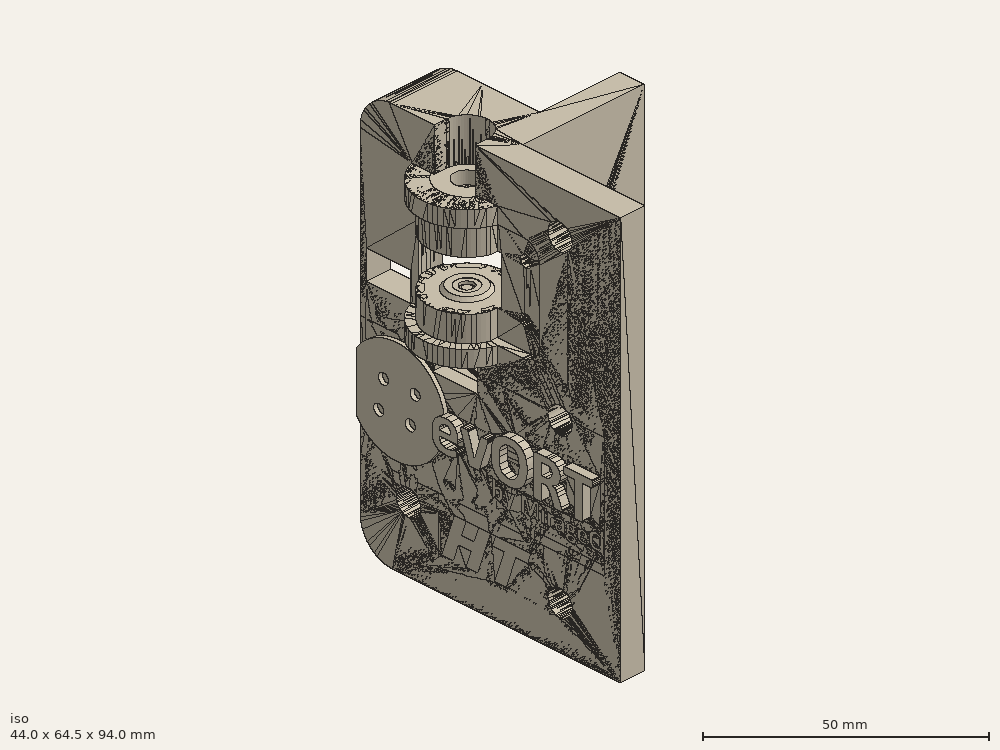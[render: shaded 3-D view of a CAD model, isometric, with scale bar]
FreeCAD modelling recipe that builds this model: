
FCSTD DOCUMENT  (FreeCAD 0.18R16146 (Git))
Label: front-idler-left-2
License: All rights reserved
LicenseURL: http://en.wikipedia.org/wiki/All_rights_reserved
objects: Part::Cylinder×11, Part::Cut×9, Part::Box×8, Part::MultiFuse×8, Part::Chamfer×5, Part::Feature×4
note: 45 computed .brp shape members not serialized (recipe doc carries the construction recipe); baked Part::Feature solids carry a one-line shape summary decoded from their .brp

FEATURE [Part::Feature] Part__Feature  label="PulleyMount_FRONT_LEFT_BodyV1.1"
  Placement = pos=(30,-2.64,-428.83) rot=(1,0,0;1.5708rad)
  shape: bbox 44 x 64.5 x 93.95 mm, 768 faces (baked)
FEATURE [Part::Box] Box  label="Cube"
  AttacherType = Attacher::AttachEngine3D
  Height = 10
  Length = 10
  Placement = pos=(0,7.92,20) rot=(0,0,1;0rad)
  Width = 12
FEATURE [Part::Feature] Part__Feature001  label="PulleyMount_FRONT_LEFT_BodyV1.002"
  shape: bbox 44 x 64.5 x 93.95 mm, 768 faces (baked)
FEATURE [Part::Cut] Cut
  Base = -> Part__Feature001
  Tool = -> Box
FEATURE [Part::Box] Box002  label="Cube002"
  AttacherType = Attacher::AttachEngine3D
  Height = 29
  Length = 3
  Placement = pos=(-1,-8.1,14) rot=(0,0,1;0rad)
  Width = 6.2
FEATURE [Part::Box] Box003  label="Cube003"
  AttacherType = Attacher::AttachEngine3D
  Height = 29
  Length = 3
  Placement = pos=(-1,-8.1,51) rot=(0,0,1;0rad)
  Width = 6.2
FEATURE [Part::Box] Box004  label="Cube004"
  AttacherType = Attacher::AttachEngine3D
  Height = 6.4
  Length = 3
  Placement = pos=(-1,11,12) rot=(0,0,1;0rad)
  Width = 16
FEATURE [Part::Cylinder] Cylinder  label="pos"
  Angle = 360
  AttacherType = Attacher::AttachEngine3D
  Height = 10
  Placement = pos=(-3,20.86,51.94) rot=(0,0,1;0rad)
  Radius = 1
FEATURE [Part::Cylinder] Cylinder001  label="pos001"
  Angle = 360
  AttacherType = Attacher::AttachEngine3D
  Height = 9.75
  Placement = pos=(-3,20.86,51.94) rot=(0,0,1;0rad)
  Radius = 5.54
FEATURE [Part::MultiFuse] Fusion
  Shapes = -> [Cylinder001,Cut]
FEATURE [Part::Cylinder] Cylinder002  label="pos002"
  Angle = 360
  AttacherType = Attacher::AttachEngine3D
  Height = 10.75
  Placement = pos=(-3,20.86,73.2) rot=(0,0,1;0rad)
  Radius = 6.54
FEATURE [Part::MultiFuse] Fusion001
  Shapes = -> [Fusion,Cylinder002]
FEATURE [Part::Cylinder] Cylinder003  label="pos003"
  Angle = 360
  AttacherType = Attacher::AttachEngine3D
  Height = 3
  Placement = pos=(-3,20.86,61.69) rot=(0,0,1;0rad)
  Radius = 7.54
FEATURE [Part::Cylinder] Cylinder004  label="pos004"
  Angle = 360
  AttacherType = Attacher::AttachEngine3D
  Height = 3
  Placement = pos=(-3,20.86,70.19) rot=(0,0,1;0rad)
  Radius = 7.54
FEATURE [Part::Cut] Cut001
  Base = -> Fusion001
  Tool = -> Cylinder003
FEATURE [Part::Cut] Cut002
  Base = -> Cut001
  Tool = -> Cylinder004
FEATURE [Part::Cylinder] Cylinder005  label="pos005"
  Angle = 360
  AttacherType = Attacher::AttachEngine3D
  Height = 4
  Placement = pos=(-3,20.86,80.94) rot=(0,0,1;0rad)
  Radius = 3
FEATURE [Part::Cylinder] Cylinder006  label="pos006"
  Angle = 360
  AttacherType = Attacher::AttachEngine3D
  Height = 43
  Placement = pos=(-3,20.86,48.94) rot=(0,0,1;0rad)
  Radius = 1.6
FEATURE [Part::Feature] Body001
  Placement = pos=(-3,20.86,51.94) rot=(0,0,1;0rad)
  shape: bbox 5.543 x 6.4 x 3 mm, 8 faces (baked)
FEATURE [Part::Cut] Cut003
  Base = -> Cut002
  Tool = -> Body001
FEATURE [Part::Cut] Cut004
  Base = -> Cut003
  Tool = -> Cylinder006
FEATURE [Part::Cut] Cut005
  Base = -> Cut004
  Tool = -> Cylinder005
FEATURE [Part::Box] Box005  label="Cube005"
  AttacherType = Attacher::AttachEngine3D
  Height = 7
  Length = 5
  Placement = pos=(-6,-16,22) rot=(0,0,1;0rad)
  Width = 29
FEATURE [Part::MultiFuse] Fusion003
  Shapes = -> [Box005,Cut005]
FEATURE [Part::Cylinder] Cylinder007  label="pos007"
  Angle = 360
  AttacherType = Attacher::AttachEngine3D
  Height = 0.75
  Placement = pos=(-3,20.86,121.94) rot=(0,0,1;0rad)
  Radius = 1.6
FEATURE [Part::Cylinder] Cylinder008  label="pos008"
  Angle = 360
  AttacherType = Attacher::AttachEngine3D
  Height = 0.75
  Placement = pos=(-3,20.86,121.94) rot=(0,0,1;0rad)
  Radius = 3.5
FEATURE [Part::Cut] Cut006
  Base = -> Cylinder008
  Placement = pos=(0,0,-60.25) rot=(0,0,1;0rad)
  Tool = -> Cylinder007
FEATURE [Part::Feature] Cut006001  label="Cut007"
  Placement = pos=(0,0,-49.5) rot=(0,0,1;0rad)
  shape: bbox 7 x 7 x 0.75 mm, 4 faces (baked)
FEATURE [Part::Chamfer] Chamfer005
  Base = -> Cut006001
  Edges = 1 edges r=0.5: [Edge3]
  Placement = pos=(0,0,0.1) rot=(0,0,1;0rad)
FEATURE [Part::Chamfer] Chamfer006
  Base = -> Cut006
  Edges = 1 edges r=0.5: [Edge1]
  Placement = pos=(0,0,-0.1) rot=(0,0,1;0rad)
FEATURE [Part::MultiFuse] Fusion004
  Shapes = -> [Fusion003,Chamfer005,Chamfer006]
FEATURE [Part::Chamfer] Chamfer
  Base = -> Box004
  Edges = 1 edges r=2: [Edge6]
FEATURE [Part::Chamfer] Chamfer007
  Base = -> Box002
  Edges = 1 edges r=2: [Edge6]
FEATURE [Part::Chamfer] Chamfer008
  Base = -> Box003
  Edges = 1 edges r=2: [Edge6]
FEATURE [Part::MultiFuse] Fusion005
  Shapes = -> [Chamfer008,Chamfer007,Chamfer]
FEATURE [Part::Cylinder] Cylinder009  label="pos009"
  Angle = 360
  AttacherType = Attacher::AttachEngine3D
  Height = 6
  Placement = pos=(-3,20.86,51.94) rot=(0,0,1;0rad)
  Radius = 2.1
FEATURE [Part::Cylinder] Cylinder010  label="pos010"
  Angle = 360
  AttacherType = Attacher::AttachEngine3D
  Height = 6
  Placement = pos=(-3,20.86,51.94) rot=(0,0,1;0rad)
  Radius = 3.6
FEATURE [Part::MultiFuse] Fusion006
  Shapes = -> [Fusion004,Cylinder010]
FEATURE [Part::Cut] Cut006002
  Base = -> Fusion006
  Tool = -> Cylinder009
FEATURE [Part::Box] Box006  label="Cube006"
  AttacherType = Attacher::AttachEngine3D
  Height = 28
  Length = 10
  Placement = pos=(-16,-16,20) rot=(0,0,1;0rad)
  Width = 62
FEATURE [Part::Cut] Cut006003
  Base = -> Cut006002
  Tool = -> Box006
FEATURE [Part::Box] Box007  label="Cube007"
  AttacherType = Attacher::AttachEngine3D
  Height = 14
  Length = 3
  Placement = pos=(-6,28,27) rot=(0,0,1;0rad)
  Width = 13
FEATURE [Part::MultiFuse] Fusion007
  Shapes = -> [Box007,Cut006003]
FEATURE [Part::Box] Box008  label="Cube008"
  AttacherType = Attacher::AttachEngine3D
  Height = 15
  Length = 3
  Placement = pos=(-6,-1,5) rot=(0,0,1;0rad)
  Width = 26
FEATURE [Part::MultiFuse] Fusion008
  Shapes = -> [Box008,Fusion007]
